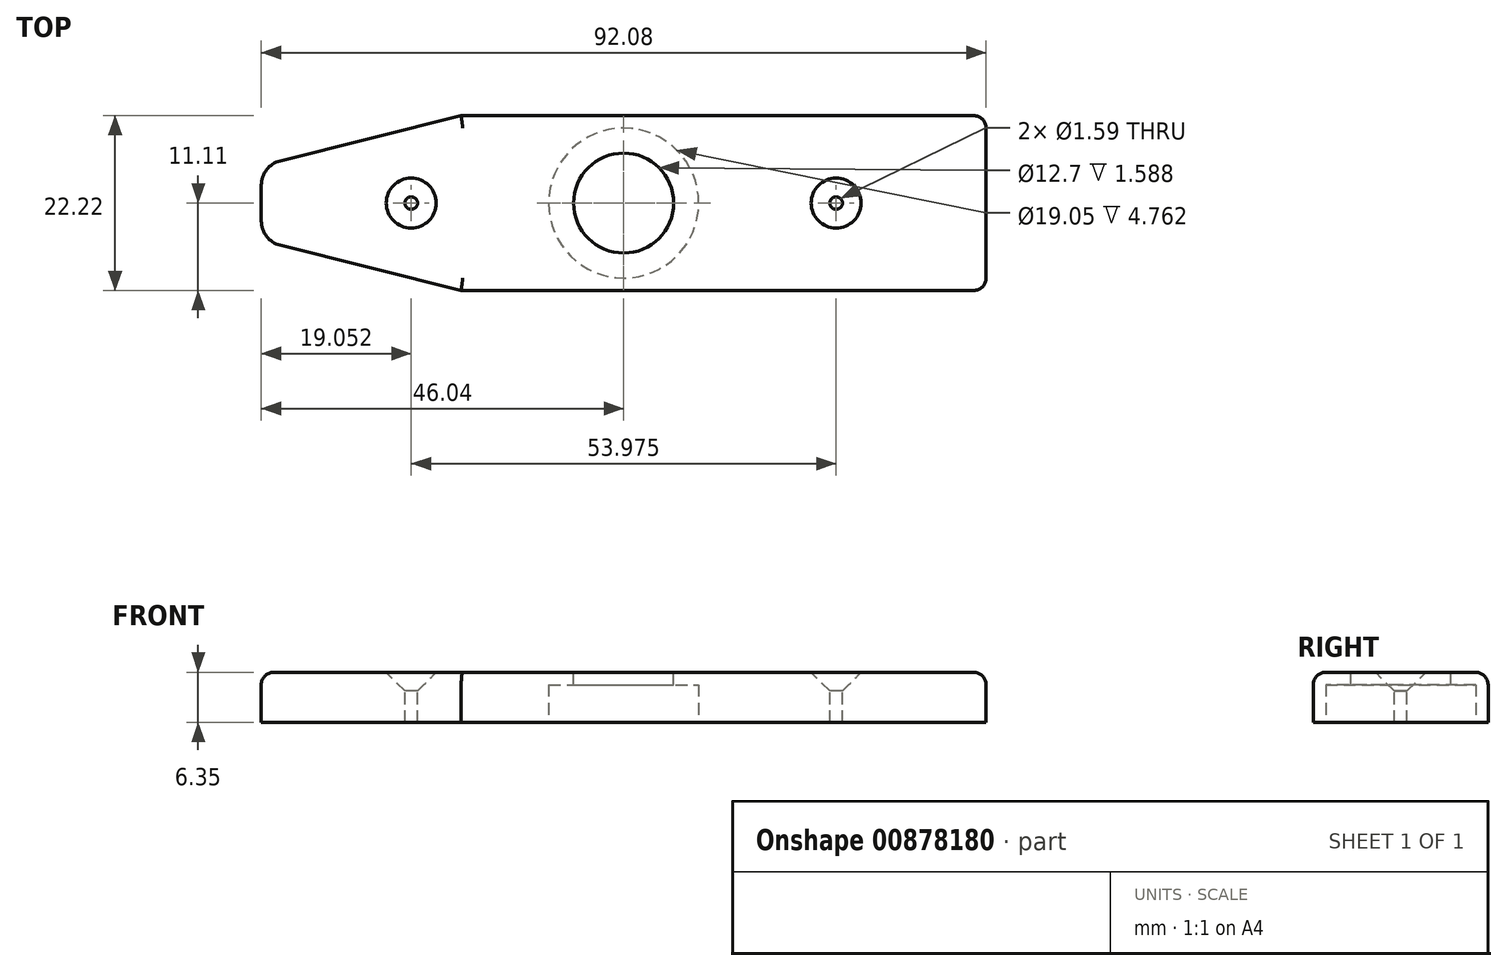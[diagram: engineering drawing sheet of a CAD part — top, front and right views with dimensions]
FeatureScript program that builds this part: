
annotation { "Feature Type Name" : "Feature", "Feature Type Description" : "" }
export const myFeature = defineFeature(function(context is Context, id is Id, definition is map)
    precondition{}
    {
        {
            var Q0;
            Q0=qCreatedBy(makeId("Top.planeOp"),FACE);
            var sketch = newSketch(context, id + "F0", { "sketchPlane" : qUnion([Q0])});
            skLineSegment(sketch, "E0.bottom", {"start": v(46.04, -11.11) * mm, "end": v(-46.04, -11.11) * mm});
            skLineSegment(sketch, "E0.top", {"start": v(46.04, 11.11) * mm, "end": v(-46.04, 11.11) * mm});
            skLineSegment(sketch, "E0.left", {"start": v(46.04, -11.11) * mm, "end": v(46.04, 11.11) * mm});
            skLineSegment(sketch, "E0.right", {"start": v(-46.04, -11.11) * mm, "end": v(-46.04, 11.11) * mm});
            skCircle(sketch, "E1", {"center": v(0, 0) * mm, "radius": 6.35 * mm});
            skSolve(sketch);
        }
        {
            var Q0;
            Q0 = qSketchRegion(id + "F0", true);
            extrude(context, id + "F1", {"entities" : qUnion([Q0]), "oppositeDirection" : true, "depth" : 6.35 * mm, "offsetDistance" : 25.4 * mm});
        }
        {
            var Q0;
            Q0=qCreatedBy(makeId("Top.planeOp"),FACE);
            var sketch = newSketch(context, id + "F2", { "sketchPlane" : qUnion([Q0])});
            skCircle(sketch, "E2", {"center": v(-26.99, 0) * mm, "radius": 0.8 * mm});
            skCircle(sketch, "E3.MirrorC", {"center": v(26.99, 0) * mm, "radius": 0.8 * mm});
            skSolve(sketch);
        }
        {
            var Q0;
            Q0=sQuery(id+"F2.wireOp",VERTEX,"E3.MirrorC.center");
            var Q1;
            Q1=sQuery(id+"F2.wireOp",VERTEX,"E2.center");
            var Q2;
            Q2=makeQuery(id+"F1.opExtrude","SWEPT_BODY",BODY,{"disambiguationData":[OSD([sQuery(id+"F0.wireOp",EDGE,"E0.bottom"),sQuery(id+"F0.wireOp",EDGE,"E0.top"),sQuery(id+"F0.wireOp",EDGE,"E0.left"),sQuery(id+"F0.wireOp",EDGE,"E0.right"),sQuery(id+"F0.wireOp",EDGE,"E1")])]});
            hole(context, id + "F3", {"style" : HoleStyle.C_SINK, "endStyle" : HoleEndStyle.THROUGH, "holeDiameter" : 1.59 * mm, "cSinkDiameter" : 6.35 * mm, "cSinkAngle" : 90 * degree, "majorDiameter" : 6.35 * mm, "isTappedThrough" : true, "tappedDepth" : 12.7 * mm, "tapClearance" : 3, "startFromSketch" : true, "locations" : qUnion([Q0, Q1]), "scope" : qUnion([Q2])});
        }
        {
            var Q0;
            Q0=qCreatedBy(makeId("Top.planeOp"),FACE);
            cPlane(context, id + "F4", {"entities" : qUnion([Q0]), "cplaneType" : CPlaneType.OFFSET, "offset" : 6.35 * mm, "oppositeDirection" : true, "width" : 152.4 * mm, "height" : 152.4 * mm});
        }
        {
            var Q0;
            Q0=qCreatedBy(id+"F4.planeOp",FACE);
            var sketch = newSketch(context, id + "F5", { "sketchPlane" : qUnion([Q0])});
            skCircle(sketch, "E4", {"center": v(0, 0) * mm, "radius": 9.53 * mm});
            skSolve(sketch);
        }
        {
            var Q0;
            Q0=sQuery(id+"F5.wireOp",VERTEX,"E4.center");
            var Q1;
            Q1=makeQuery(id+"F1.opExtrude","SWEPT_BODY",BODY,{"disambiguationData":[OSD([sQuery(id+"F0.wireOp",EDGE,"E0.bottom"),sQuery(id+"F0.wireOp",EDGE,"E0.top"),sQuery(id+"F0.wireOp",EDGE,"E0.left"),sQuery(id+"F0.wireOp",EDGE,"E0.right"),sQuery(id+"F0.wireOp",EDGE,"E1")])]});
            hole(context, id + "F6", {"style" : HoleStyle.C_BORE, "endStyle" : HoleEndStyle.THROUGH, "oppositeDirection" : true, "holeDiameter" : 12.7 * mm, "cBoreDiameter" : 19.05 * mm, "cBoreDepth" : 4.76 * mm, "majorDiameter" : 6.35 * mm, "isTappedThrough" : true, "tappedDepth" : 12.7 * mm, "tapClearance" : 3, "startFromSketch" : true, "locations" : qUnion([Q0]), "scope" : qUnion([Q1])});
        }
        {
            var Q0;
            Q0=makeQuery(id+"F1.opExtrude","SWEPT_EDGE",EDGE,{"disambiguationData":[OSD([sQuery(id+"F0.wireOp",EDGE,"E0.bottom"),sQuery(id+"F0.wireOp",EDGE,"E0.right")])]});
            var Q1;
            Q1=makeQuery(id+"F1.opExtrude","SWEPT_EDGE",EDGE,{"disambiguationData":[OSD([sQuery(id+"F0.wireOp",EDGE,"E0.top"),sQuery(id+"F0.wireOp",EDGE,"E0.right")])]});
            chamfer(context, id + "F7", {"entities" : qUnion([Q0, Q1]), "chamferType" : ChamferType.TWO_OFFSETS, "width1" : 6.35 * mm, "oppositeDirection" : false, "width2" : 25.4 * mm, "tangentPropagation" : true});
        }
        {
            var Q0;
            {var subQ0=sQuery(id+"F0.wireOp",EDGE,"E0.right");Q0=makeQuery(id+"F7.opChamfer","BLEND_EDGE",EDGE,{"blendedFrom":[makeQuery(id+"F1.opExtrude","SWEPT_EDGE",EDGE,{"disambiguationData":[OSD([sQuery(id+"F0.wireOp",EDGE,"E0.bottom"),subQ0])]}),makeQuery(id+"F1.opExtrude","SWEPT_FACE",FACE,{"disambiguationData":[OSD([subQ0])]})],"blendedInto":[makeQuery(id+"F1.opExtrude","SWEPT_FACE",FACE,{"disambiguationData":[OSD([subQ0])]})]});}
            var Q1;
            {var subQ0=sQuery(id+"F0.wireOp",EDGE,"E0.right");Q1=makeQuery(id+"F7.opChamfer","BLEND_EDGE",EDGE,{"blendedFrom":[makeQuery(id+"F1.opExtrude","SWEPT_EDGE",EDGE,{"disambiguationData":[OSD([sQuery(id+"F0.wireOp",EDGE,"E0.top"),subQ0])]}),makeQuery(id+"F1.opExtrude","SWEPT_FACE",FACE,{"disambiguationData":[OSD([subQ0])]})],"blendedInto":[makeQuery(id+"F1.opExtrude","SWEPT_FACE",FACE,{"disambiguationData":[OSD([subQ0])]})]});}
            fillet(context, id + "F8", {"entities" : qUnion([Q0, Q1]), "radius" : 3.17 * mm, "tangentPropagation" : true, "allowEdgeOverflow" : false});
        }
        {
            var Q0;
            Q0=makeQuery(id+"F1.opExtrude","CAP_EDGE",EDGE,{"disambiguationData":[OSD([sQuery(id+"F0.wireOp",EDGE,"E0.bottom")])],"isStart":true});
            var Q1;
            Q1=makeQuery(id+"F1.opExtrude","CAP_EDGE",EDGE,{"disambiguationData":[OSD([sQuery(id+"F0.wireOp",EDGE,"E0.left")])],"isStart":true});
            var Q2;
            Q2=makeQuery(id+"F1.opExtrude","CAP_EDGE",EDGE,{"disambiguationData":[OSD([sQuery(id+"F0.wireOp",EDGE,"E0.top")])],"isStart":true});
            var Q3;
            {var subQ0=sQuery(id+"F0.wireOp",EDGE,"E0.right");var subQ1=sQuery(id+"F0.wireOp",EDGE,"E0.bottom");Q3=makeQuery(id+"F7.opChamfer","BLEND_EDGE",EDGE,{"blendedFrom":[makeQuery(id+"F1.opExtrude","SWEPT_EDGE",EDGE,{"disambiguationData":[OSD([subQ1,subQ0])]}),makeQuery(id+"F1.opExtrude","CAP_FACE",FACE,{"disambiguationData":[OSD([subQ1,sQuery(id+"F0.wireOp",EDGE,"E0.top"),sQuery(id+"F0.wireOp",EDGE,"E0.left"),subQ0,sQuery(id+"F0.wireOp",EDGE,"E1")])],"isStart":true})],"blendedInto":[makeQuery(id+"F1.opExtrude","CAP_FACE",FACE,{"disambiguationData":[OSD([subQ1,sQuery(id+"F0.wireOp",EDGE,"E0.top"),sQuery(id+"F0.wireOp",EDGE,"E0.left"),subQ0,sQuery(id+"F0.wireOp",EDGE,"E1")])],"isStart":true})]});}
            var Q4;
            {var subQ0=sQuery(id+"F0.wireOp",EDGE,"E0.right");var subQ1=sQuery(id+"F0.wireOp",EDGE,"E0.top");Q4=makeQuery(id+"F7.opChamfer","BLEND_EDGE",EDGE,{"blendedFrom":[makeQuery(id+"F1.opExtrude","SWEPT_EDGE",EDGE,{"disambiguationData":[OSD([subQ1,subQ0])]}),makeQuery(id+"F1.opExtrude","CAP_FACE",FACE,{"disambiguationData":[OSD([sQuery(id+"F0.wireOp",EDGE,"E0.bottom"),subQ1,sQuery(id+"F0.wireOp",EDGE,"E0.left"),subQ0,sQuery(id+"F0.wireOp",EDGE,"E1")])],"isStart":true})],"blendedInto":[makeQuery(id+"F1.opExtrude","CAP_FACE",FACE,{"disambiguationData":[OSD([sQuery(id+"F0.wireOp",EDGE,"E0.bottom"),subQ1,sQuery(id+"F0.wireOp",EDGE,"E0.left"),subQ0,sQuery(id+"F0.wireOp",EDGE,"E1")])],"isStart":true})]});}
            var Q5;
            {var subQ0=sQuery(id+"F0.wireOp",EDGE,"E0.right");var subQ1=sQuery(id+"F0.wireOp",EDGE,"E0.top");Q5=makeQuery(id+"F8.opFillet","BLEND_EDGE",EDGE,{"blendedFrom":[makeQuery(id+"F7.opChamfer","BLEND_EDGE",EDGE,{"blendedFrom":[makeQuery(id+"F1.opExtrude","SWEPT_EDGE",EDGE,{"disambiguationData":[OSD([subQ1,subQ0])]}),makeQuery(id+"F1.opExtrude","SWEPT_FACE",FACE,{"disambiguationData":[OSD([subQ0])]})],"blendedInto":[makeQuery(id+"F1.opExtrude","SWEPT_FACE",FACE,{"disambiguationData":[OSD([subQ0])]})]}),makeQuery(id+"F1.opExtrude","CAP_FACE",FACE,{"disambiguationData":[OSD([sQuery(id+"F0.wireOp",EDGE,"E0.bottom"),subQ1,sQuery(id+"F0.wireOp",EDGE,"E0.left"),subQ0,sQuery(id+"F0.wireOp",EDGE,"E1")])],"isStart":true})],"blendedInto":[makeQuery(id+"F1.opExtrude","CAP_FACE",FACE,{"disambiguationData":[OSD([sQuery(id+"F0.wireOp",EDGE,"E0.bottom"),subQ1,sQuery(id+"F0.wireOp",EDGE,"E0.left"),subQ0,sQuery(id+"F0.wireOp",EDGE,"E1")])],"isStart":true})]});}
            var Q6;
            Q6=makeQuery(id+"F1.opExtrude","CAP_EDGE",EDGE,{"disambiguationData":[OSD([sQuery(id+"F0.wireOp",EDGE,"E0.right")])],"isStart":true});
            var Q7;
            {var subQ0=sQuery(id+"F0.wireOp",EDGE,"E0.right");var subQ1=sQuery(id+"F0.wireOp",EDGE,"E0.bottom");Q7=makeQuery(id+"F8.opFillet","BLEND_EDGE",EDGE,{"blendedFrom":[makeQuery(id+"F7.opChamfer","BLEND_EDGE",EDGE,{"blendedFrom":[makeQuery(id+"F1.opExtrude","SWEPT_EDGE",EDGE,{"disambiguationData":[OSD([subQ1,subQ0])]}),makeQuery(id+"F1.opExtrude","SWEPT_FACE",FACE,{"disambiguationData":[OSD([subQ0])]})],"blendedInto":[makeQuery(id+"F1.opExtrude","SWEPT_FACE",FACE,{"disambiguationData":[OSD([subQ0])]})]}),makeQuery(id+"F1.opExtrude","CAP_FACE",FACE,{"disambiguationData":[OSD([subQ1,sQuery(id+"F0.wireOp",EDGE,"E0.top"),sQuery(id+"F0.wireOp",EDGE,"E0.left"),subQ0,sQuery(id+"F0.wireOp",EDGE,"E1")])],"isStart":true})],"blendedInto":[makeQuery(id+"F1.opExtrude","CAP_FACE",FACE,{"disambiguationData":[OSD([subQ1,sQuery(id+"F0.wireOp",EDGE,"E0.top"),sQuery(id+"F0.wireOp",EDGE,"E0.left"),subQ0,sQuery(id+"F0.wireOp",EDGE,"E1")])],"isStart":true})]});}
            var Q8;
            Q8=makeQuery(id+"F1.opExtrude","SWEPT_EDGE",EDGE,{"disambiguationData":[OSD([sQuery(id+"F0.wireOp",EDGE,"E0.bottom"),sQuery(id+"F0.wireOp",EDGE,"E0.left")])]});
            var Q9;
            Q9=makeQuery(id+"F1.opExtrude","SWEPT_EDGE",EDGE,{"disambiguationData":[OSD([sQuery(id+"F0.wireOp",EDGE,"E0.top"),sQuery(id+"F0.wireOp",EDGE,"E0.left")])]});
            fillet(context, id + "F9", {"entities" : qUnion([Q0, Q1, Q2, Q3, Q4, Q5, Q6, Q7, Q8, Q9]), "radius" : 1.59 * mm, "tangentPropagation" : true, "allowEdgeOverflow" : false});
        }
    });
